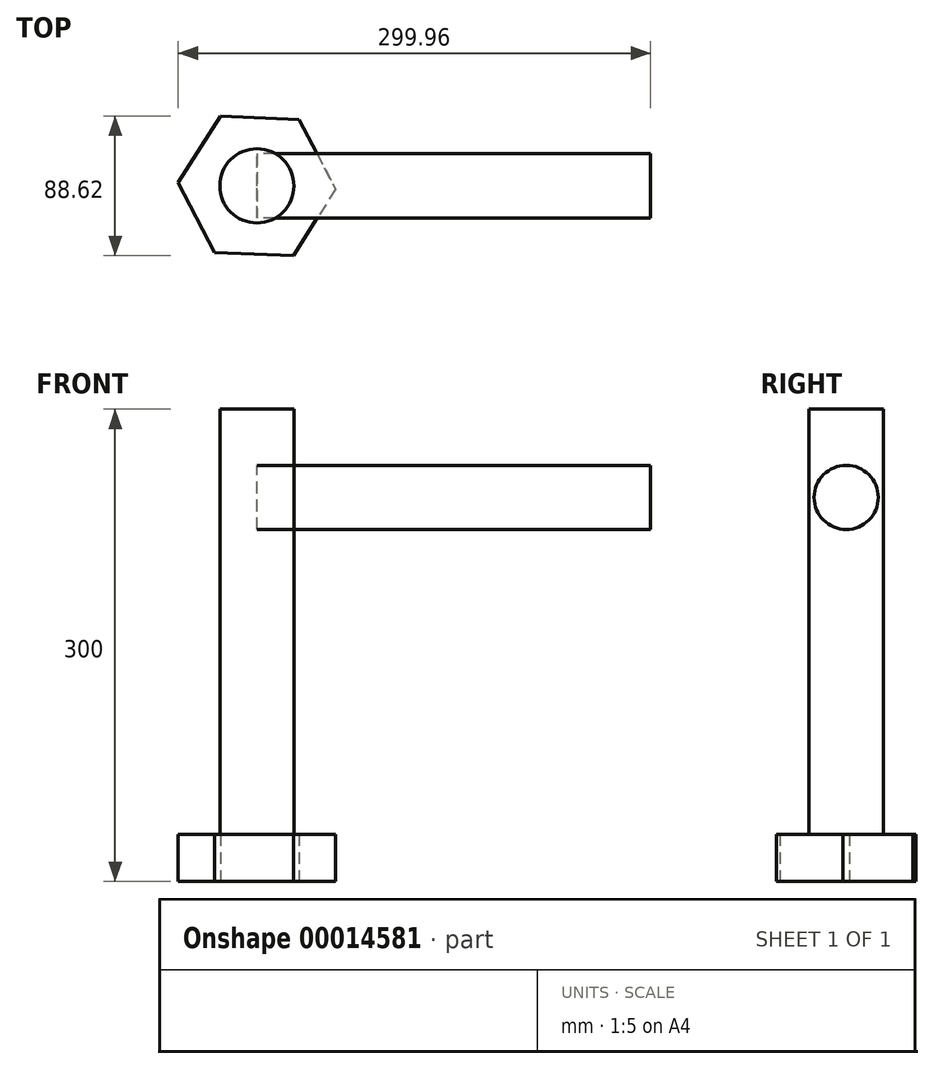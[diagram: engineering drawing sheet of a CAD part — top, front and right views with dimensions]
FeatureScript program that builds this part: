
annotation { "Feature Type Name" : "Feature", "Feature Type Description" : "" }
export const myFeature = defineFeature(function(context is Context, id is Id, definition is map)
    precondition{}
    {
        {
            var Q0;
            Q0=qCreatedBy(makeId("Top.planeOp"),FACE);
            var sketch = newSketch(context, id + "F0", { "sketchPlane" : qUnion([Q0])});
            skCircle(sketch, "E0.cCircle", {"center": v(0, 0) * mm, "radius": 50 * mm, "construction": true});
            skLineSegment(sketch, "E0.0", {"start": v(26.79, 42.22) * mm, "end": v(49.96, -2.09) * mm});
            skLineSegment(sketch, "E0.1", {"start": v(49.96, -2.09) * mm, "end": v(23.17, -44.3) * mm});
            skLineSegment(sketch, "E0.2", {"start": v(23.17, -44.3) * mm, "end": v(-26.79, -42.22) * mm});
            skLineSegment(sketch, "E0.3", {"start": v(-26.79, -42.22) * mm, "end": v(-49.96, 2.09) * mm});
            skLineSegment(sketch, "E0.4", {"start": v(-49.96, 2.09) * mm, "end": v(-23.17, 44.3) * mm});
            skLineSegment(sketch, "E0.5", {"start": v(-23.17, 44.3) * mm, "end": v(26.79, 42.22) * mm});
            skSolve(sketch);
        }
        {
            var Q0;
            Q0=makeQuery(id+"F0.imprint","IMPRINT",FACE,{"disambiguationData":[TD([[makeQuery(id+"F0.imprint","IMPRINT",EDGE,{"derivedFrom":sQuery(id+"F0.wireOp",EDGE,"E0.0")}),-1.0]])]});
            extrude(context, id + "F4", {"entities" : qUnion([Q0]), "depth" : 30 * mm});
        }
        {
            var Q0;
            Q0=qCreatedBy(makeId("Top.planeOp"),FACE);
            var sketch = newSketch(context, id + "F1", { "sketchPlane" : qUnion([Q0])});
            skCircle(sketch, "E1", {"center": v(0, 0) * mm, "radius": 23.53 * mm});
            skSolve(sketch);
        }
        {
            var Q0;
            Q0=makeQuery(id+"F1.imprint","IMPRINT",FACE,{"disambiguationData":[TD([[makeQuery(id+"F1.imprint","IMPRINT",EDGE,{"derivedFrom":sQuery(id+"F1.wireOp",EDGE,"E1")}),1.0]])]});
            extrude(context, id + "F2", {"entities" : qUnion([Q0]), "operationType" : NewBodyOperationType.ADD, "depth" : 300 * mm});
        }
        {
            var Q0;
            Q0=qCreatedBy(makeId("Right.planeOp"),FACE);
            var sketch = newSketch(context, id + "F5", { "sketchPlane" : qUnion([Q0])});
            skCircle(sketch, "E2", {"center": v(0, 243.92) * mm, "radius": 20.38 * mm});
            skSolve(sketch);
        }
        {
            var Q0;
            Q0=makeQuery(id+"F5.imprint","IMPRINT",FACE,{"disambiguationData":[TD([[makeQuery(id+"F5.imprint","IMPRINT",EDGE,{"derivedFrom":sQuery(id+"F5.wireOp",EDGE,"E2")}),1.0]])]});
            extrude(context, id + "F3", {"entities" : qUnion([Q0]), "depth" : 250 * mm});
        }
    });
